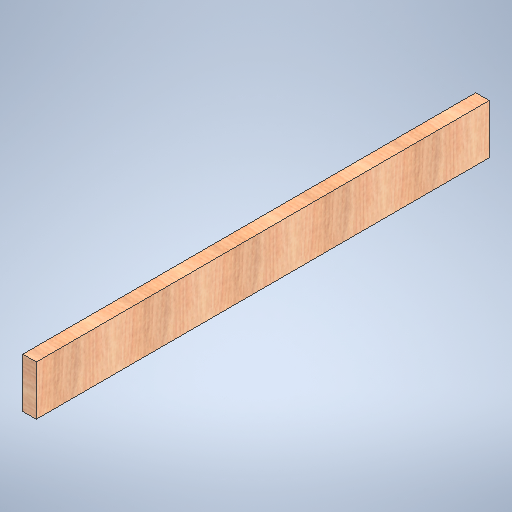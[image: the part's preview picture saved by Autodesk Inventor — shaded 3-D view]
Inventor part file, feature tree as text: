
AUTODESK INVENTOR PART (.ipt)
format: ipt  version: 2025.1 (Build 291241020, 241B)  size: 326,144 bytes
history: native  units: in
note: dims shown in document units (in); Inventor stores cm internally (conversion verified against a paired STEP export)
features: extrude x1, sketch x1
ambient origin geometry x8: Origin, YZ Plane, XZ Plane, XY Plane, X Axis, Y Axis, Z Axis, Center Point
bodies: Solid1 (feature_tree)
feature tree (2):
  extrude  "Extrusion1"  Depth=1.5in TaperAngle=0.0deg
  sketch  "Sketch1"  dims[d1=50.25in d2=1.5in d3=0.0in d4=5.5in]
